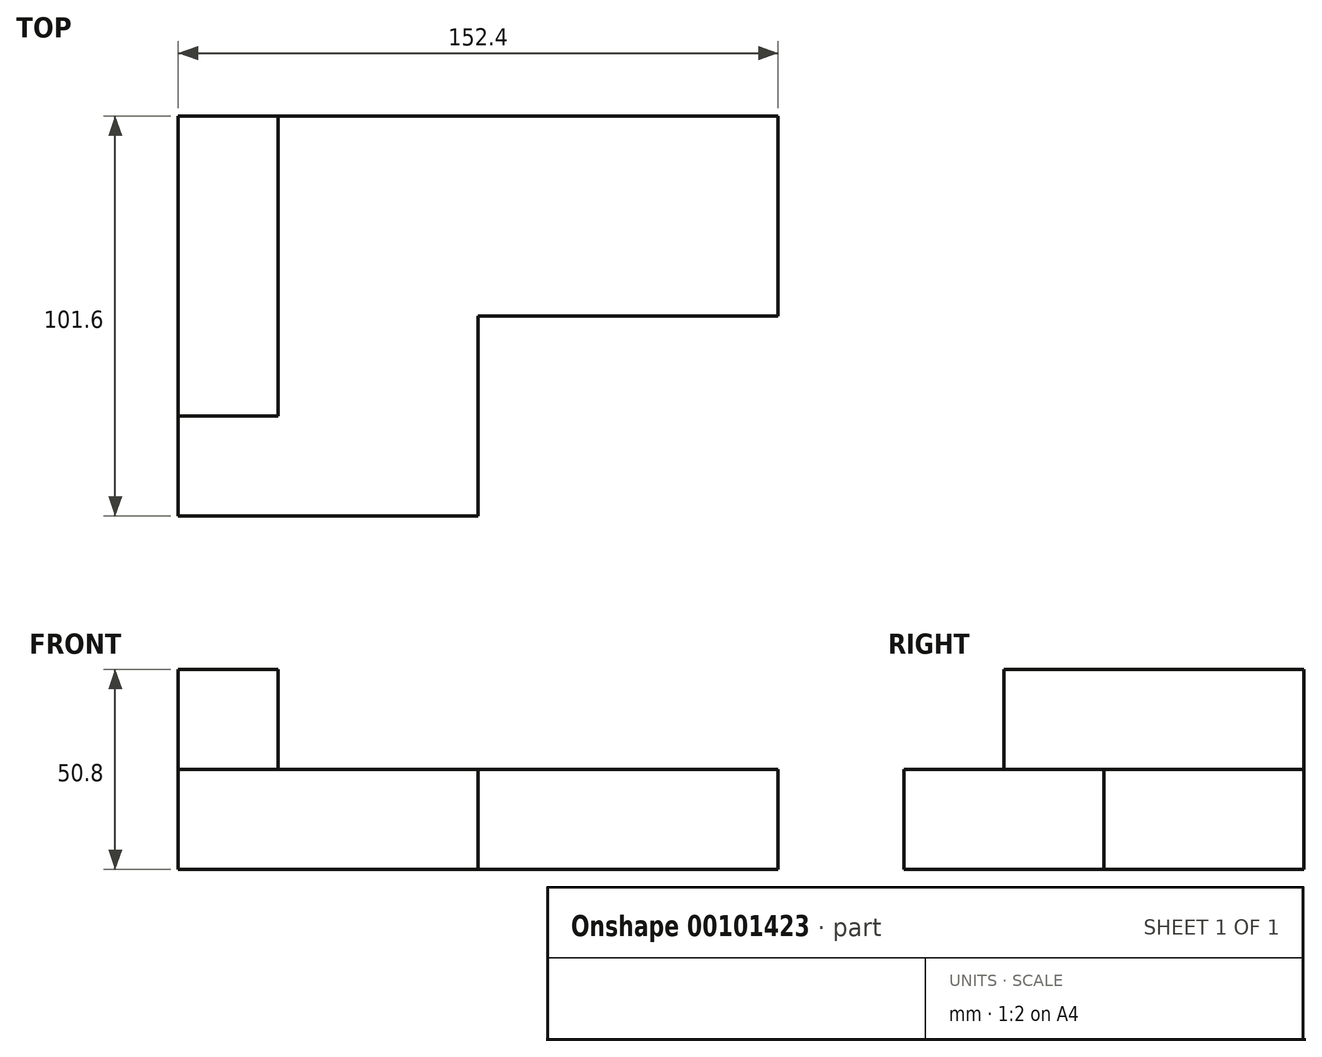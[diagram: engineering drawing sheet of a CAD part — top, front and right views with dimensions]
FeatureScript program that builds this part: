
annotation { "Feature Type Name" : "Feature", "Feature Type Description" : "" }
export const myFeature = defineFeature(function(context is Context, id is Id, definition is map)
    precondition{}
    {
        {
            var Q0;
            Q0=qCreatedBy(makeId("Top.planeOp"),FACE);
            var sketch = newSketch(context, id + "F0", { "sketchPlane" : qUnion([Q0])});
            skLineSegment(sketch, "E0", {"start": v(-146.07, 90.7) * mm, "end": v(-146.07, -10.9) * mm});
            skLineSegment(sketch, "E1", {"start": v(-146.07, -10.9) * mm, "end": v(-69.87, -10.9) * mm});
            skLineSegment(sketch, "E2", {"start": v(-69.87, -10.9) * mm, "end": v(-69.87, 39.9) * mm});
            skLineSegment(sketch, "E3", {"start": v(-69.87, 39.9) * mm, "end": v(6.33, 39.9) * mm});
            skLineSegment(sketch, "E4", {"start": v(6.33, 39.9) * mm, "end": v(6.33, 90.7) * mm});
            skLineSegment(sketch, "E5", {"start": v(6.33, 90.7) * mm, "end": v(-146.07, 90.7) * mm});
            skSolve(sketch);
        }
        {
            var Q0;
            Q0=makeQuery(id+"F0.imprint","IMPRINT",FACE,{"disambiguationData":[TD([[makeQuery(id+"F0.imprint","IMPRINT",EDGE,{"derivedFrom":sQuery(id+"F0.wireOp",EDGE,"E0")}),1.0]])]});
            extrude(context, id + "F1", {"entities" : qUnion([Q0]), "depth" : 25.4 * mm});
        }
        {
            var Q0;
            Q0=makeQuery(id+"F1.opExtrude","SWEPT_FACE",FACE,{"disambiguationData":[OSD([sQuery(id+"F0.wireOp",EDGE,"E0")])]});
            var sketch = newSketch(context, id + "F2", { "sketchPlane" : qUnion([Q0])});
            skLineSegment(sketch, "E6", {"start": v(-90.7, 0) * mm, "end": v(-90.7, 50.8) * mm});
            skLineSegment(sketch, "E7", {"start": v(-90.7, 50.8) * mm, "end": v(-14.5, 50.8) * mm});
            skLineSegment(sketch, "E8", {"start": v(-14.5, 50.8) * mm, "end": v(-14.5, 0) * mm});
            skLineSegment(sketch, "E9", {"start": v(-14.5, 0) * mm, "end": v(-90.7, 0) * mm});
            skSolve(sketch);
        }
        {
            var Q0;
            {var subQ3=sQuery(id+"F2.wireOp",EDGE,"E7");Q0=makeQuery(id+"F2.imprint","IMPRINT",FACE,{"disambiguationData":[TD([[makeQuery(id+"F2.imprint","IMPRINT",EDGE,{"derivedFrom":subQ3}),-1.0]])]});}
            extrude(context, id + "F3", {"entities" : qUnion([Q0]), "operationType" : NewBodyOperationType.ADD, "oppositeDirection" : true, "depth" : 25.4 * mm});
        }
    });
